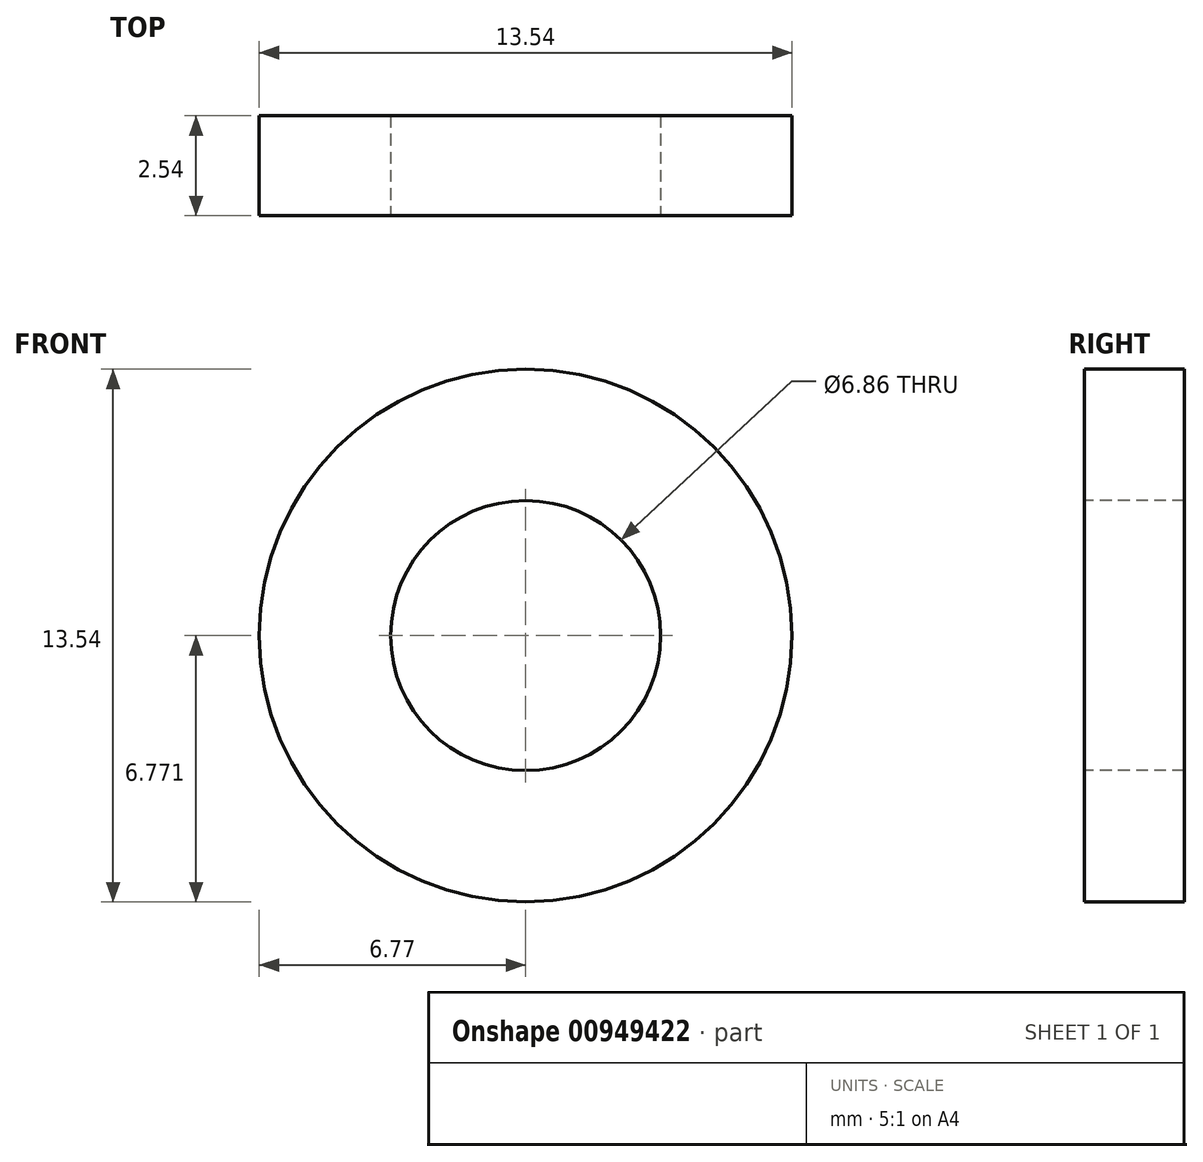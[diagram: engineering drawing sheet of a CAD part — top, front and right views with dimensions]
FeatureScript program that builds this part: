
annotation { "Feature Type Name" : "Feature", "Feature Type Description" : "" }
export const myFeature = defineFeature(function(context is Context, id is Id, definition is map)
    precondition{}
    {
        {
            var Q0;
            Q0=qCreatedBy(makeId("Front.planeOp"),FACE);
            cPlane(context, id + "F0", {"entities" : qUnion([Q0]), "cplaneType" : CPlaneType.OFFSET, "offset" : 25.4 * mm, "width" : 152.4 * mm, "height" : 152.4 * mm});
        }
        {
            var Q0;
            Q0=qCreatedBy(id+"F0.planeOp",FACE);
            var sketch = newSketch(context, id + "F1", { "sketchPlane" : qUnion([Q0])});
            skLineSegment(sketch, "E0.bottom", {"start": v(-6.72, -156.46) * mm, "end": v(0, -156.46) * mm});
            skLineSegment(sketch, "E0.top", {"start": v(-6.72, -156.46) * mm, "end": v(0, -156.46) * mm});
            skLineSegment(sketch, "E0.right", {"start": v(0, 0) * mm, "end": v(0, 0) * mm});
            skLineSegment(sketch, "E1.left", {"start": v(-6.72, -156.46) * mm, "end": v(-6.72, -152.75) * mm});
            skLineSegment(sketch, "E2.bottom", {"start": v(-6.72, -152.75) * mm, "end": v(-4.84, -152.75) * mm});
            skLineSegment(sketch, "E2.top", {"start": v(-6.72, -152.75) * mm, "end": v(-4.84, -152.75) * mm});
            skLineSegment(sketch, "E3.bottom", {"start": v(-4.84, -150.86) * mm, "end": v(-1.06, -150.86) * mm});
            skLineSegment(sketch, "E3.left", {"start": v(-4.84, -150.86) * mm, "end": v(-4.84, -150.74) * mm});
            skLineSegment(sketch, "E3.right", {"start": v(-1.06, -150.86) * mm, "end": v(-1.06, -150.74) * mm});
            skLineSegment(sketch, "E4.left", {"start": v(-4.84, -150.74) * mm, "end": v(-4.84, -152.75) * mm});
            skLineSegment(sketch, "E4.right", {"start": v(-4.84, -150.74) * mm, "end": v(-4.84, -152.75) * mm});
            skCircle(sketch, "E5", {"center": v(0, 37.57) * mm, "radius": 3.43 * mm});
            skCircle(sketch, "E6", {"center": v(0, 37.57) * mm, "radius": 6.77 * mm});
            skLineSegment(sketch, "E7.MirrorCS", {"start": v(4.84, -150.74) * mm, "end": v(1.06, -150.74) * mm});
            skLineSegment(sketch, "E8.MirrorCS", {"start": v(4.84, -150.86) * mm, "end": v(4.84, -150.74) * mm});
            skLineSegment(sketch, "E9.MirrorCS", {"start": v(6.72, -152.75) * mm, "end": v(4.84, -152.75) * mm});
            skLineSegment(sketch, "E10.MirrorCS", {"start": v(6.72, -156.46) * mm, "end": v(0, -156.46) * mm});
            skLineSegment(sketch, "E11.MirrorCS", {"start": v(4.84, -150.74) * mm, "end": v(4.84, -152.75) * mm});
            skLineSegment(sketch, "E12.MirrorCS", {"start": v(6.72, -156.46) * mm, "end": v(6.72, -152.75) * mm});
            skLineSegment(sketch, "E13", {"start": v(1.06, -150.74) * mm, "end": v(1.06, 30.89) * mm});
            skLineSegment(sketch, "E14", {"start": v(-1.06, -150.74) * mm, "end": v(-1.06, 30.89) * mm});
            skSolve(sketch);
        }
        {
            var Q0;
            Q0=makeQuery(id+"F1.imprint","IMPRINT",FACE,{"disambiguationData":[TD([[makeQuery(id+"F1.imprint","IMPRINT",EDGE,{"derivedFrom":sQuery(id+"F1.wireOp",EDGE,"E0.top")}),1.0]])]});
            var Q1;
            Q1=makeQuery(id+"F1.imprint","IMPRINT",FACE,{"disambiguationData":[TD([[makeQuery(id+"F1.imprint","IMPRINT",EDGE,{"derivedFrom":sQuery(id+"F1.wireOp",EDGE,"E5")}),1.0]])]});
            var Q2;
            Q2=makeQuery(id+"F1.imprint","IMPRINT",FACE,{"disambiguationData":[TD([[makeQuery(id+"F1.imprint","IMPRINT",EDGE,{"derivedFrom":sQuery(id+"F1.wireOp",EDGE,"E5")}),-1.0]])]});
            var Q3;
            {var subQ0=sQuery(id+"F1.wireOp",EDGE,"E3.bottom");Q3=makeQuery(id+"F1.imprint","IMPRINT",FACE,{"disambiguationData":[TD([[makeQuery(id+"F1.imprint","IMPRINT",EDGE,{"derivedFrom":subQ0}),1.0]])]});}
            var Q4;
            {var subQ0=sQuery(id+"F1.wireOp",EDGE,"44471ef5-20aa-482d-b6af-e08b8e6518f614.MirrorCS");Q4=makeQuery(id+"F1.imprint","IMPRINT",FACE,{"disambiguationData":[TD([[makeQuery(id+"F1.imprint","IMPRINT",EDGE,{"derivedFrom":subQ0}),-1.0]])]});}
            extrude(context, id + "F2", {"entities" : qUnion([Q0, Q1, Q2, Q3, Q4]), "oppositeDirection" : true, "depth" : 2.54 * mm, "offsetDistance" : 25.4 * mm});
        }
        {
            var Q0;
            Q0=makeQuery(id+"F1.imprint","IMPRINT",FACE,{"disambiguationData":[TD([[makeQuery(id+"F1.imprint","IMPRINT",EDGE,{"derivedFrom":sQuery(id+"F1.wireOp",EDGE,"E5")}),1.0]])]});
            extrude(context, id + "F3", {"entities" : qUnion([Q0]), "operationType" : NewBodyOperationType.REMOVE, "oppositeDirection" : true, "depth" : 25.4 * mm, "offsetDistance" : 25.4 * mm});
        }
    });
